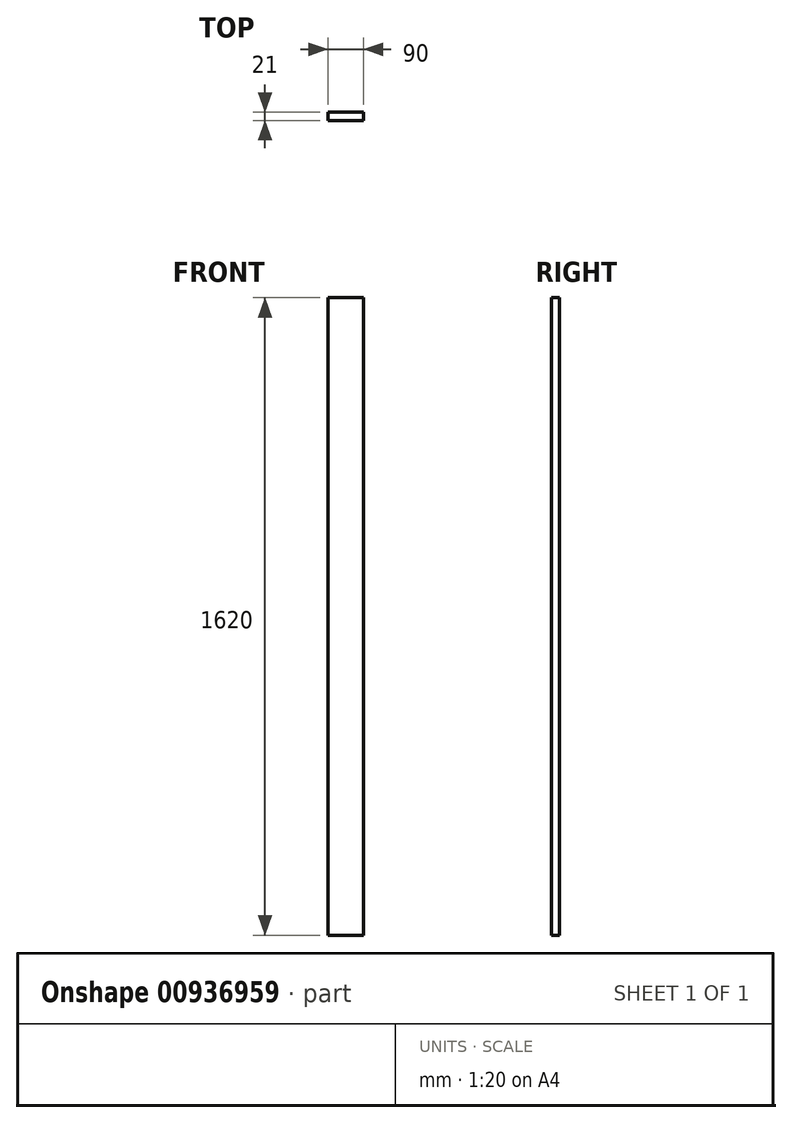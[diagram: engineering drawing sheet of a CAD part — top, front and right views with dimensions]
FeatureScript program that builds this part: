
annotation { "Feature Type Name" : "Feature", "Feature Type Description" : "" }
export const myFeature = defineFeature(function(context is Context, id is Id, definition is map)
    precondition{}
    {
        {
            var Q0;
            Q0=qCreatedBy(makeId("Top.planeOp"),FACE);
            var sketch = newSketch(context, id + "F0", { "sketchPlane" : qUnion([Q0])});
            skLineSegment(sketch, "E0.bottom", {"start": v(-45, -10.5) * mm, "end": v(45, -10.5) * mm});
            skLineSegment(sketch, "E0.top", {"start": v(-45, 10.5) * mm, "end": v(45, 10.5) * mm});
            skLineSegment(sketch, "E0.left", {"start": v(-45, -10.5) * mm, "end": v(-45, 10.5) * mm});
            skLineSegment(sketch, "E0.right", {"start": v(45, -10.5) * mm, "end": v(45, 10.5) * mm});
            skSolve(sketch);
        }
        {
            var Q0;
            Q0=makeQuery(id+"F0.imprint","IMPRINT",FACE,{"disambiguationData":[TD([[makeQuery(id+"F0.imprint","IMPRINT",EDGE,{"derivedFrom":sQuery(id+"F0.wireOp",EDGE,"E0.bottom")}),1.0]])]});
            extrude(context, id + "F1", {"entities" : qUnion([Q0]), "depth" : 1620 * mm, "offsetDistance" : 25 * mm});
        }
    });
